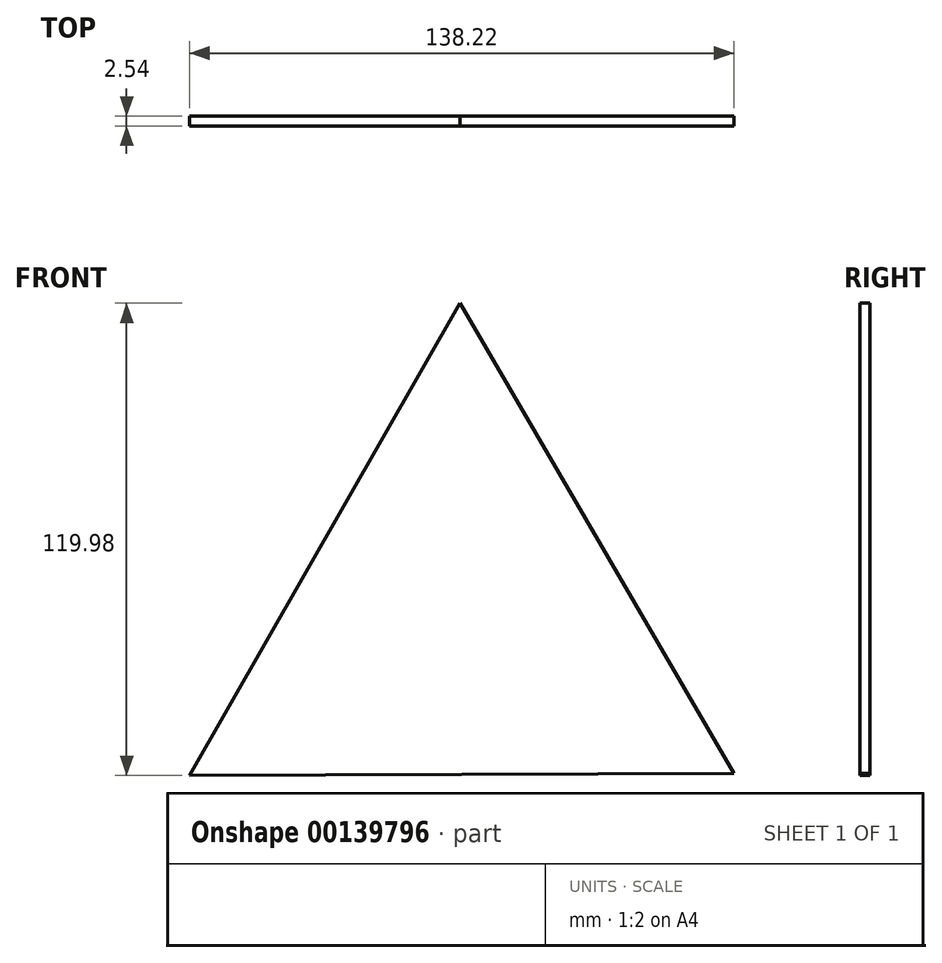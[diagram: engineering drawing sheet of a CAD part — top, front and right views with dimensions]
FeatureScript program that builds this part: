
annotation { "Feature Type Name" : "Feature", "Feature Type Description" : "" }
export const myFeature = defineFeature(function(context is Context, id is Id, definition is map)
    precondition{}
    {
        {
            var Q0;
            Q0=qCreatedBy(makeId("Front.planeOp"),FACE);
            var sketch = newSketch(context, id + "F0", { "sketchPlane" : qUnion([Q0])});
            skCircle(sketch, "E0.cCircle", {"center": v(0, 0) * mm, "radius": 39.9 * mm, "construction": true});
            skLineSegment(sketch, "E0.0", {"start": v(-0.32, 79.8) * mm, "end": v(69.27, -39.62) * mm});
            skLineSegment(sketch, "E0.1", {"start": v(69.27, -39.62) * mm, "end": v(-68.95, -40.18) * mm});
            skLineSegment(sketch, "E0.2", {"start": v(-68.95, -40.18) * mm, "end": v(-0.32, 79.8) * mm});
            skPoint(sketch, "E0.0.midPoint", {"position": v(34.47, 20.1) * mm});
            skSolve(sketch);
        }
        {
            var Q0;
            Q0=makeQuery(id+"F0.imprint","IMPRINT",FACE,{"disambiguationData":[TD([[makeQuery(id+"F0.imprint","IMPRINT",EDGE,{"derivedFrom":sQuery(id+"F0.wireOp",EDGE,"E0.0")}),-1.0]])]});
            extrude(context, id + "F1", {"entities" : qUnion([Q0]), "depth" : 2.54 * mm});
        }
    });
